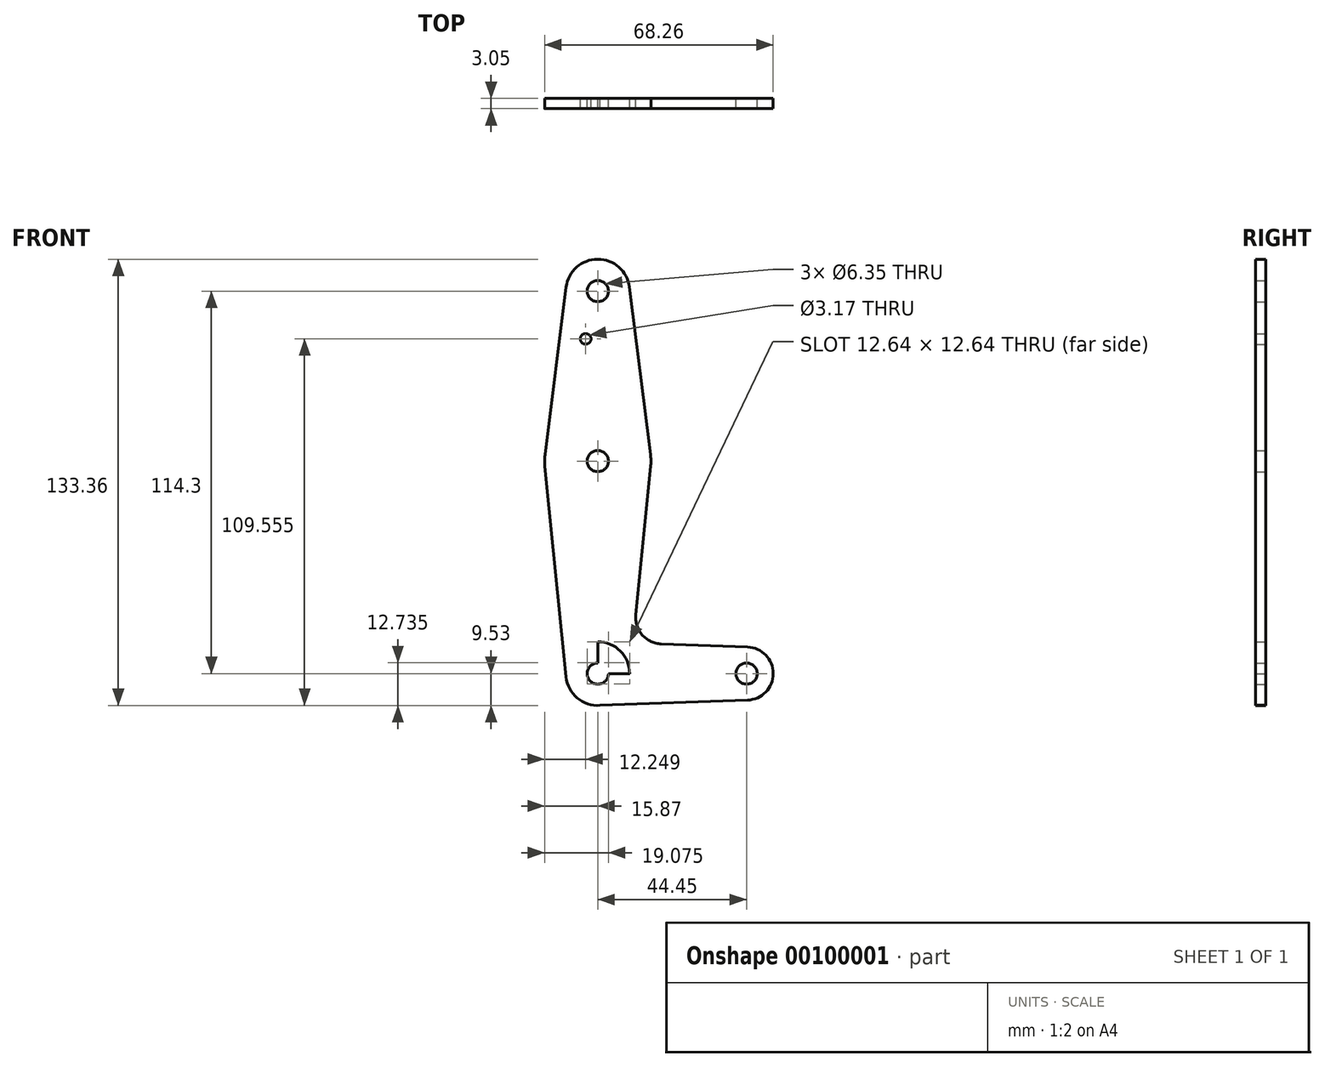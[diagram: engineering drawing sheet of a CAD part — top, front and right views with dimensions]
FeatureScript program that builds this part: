
annotation { "Feature Type Name" : "Feature", "Feature Type Description" : "" }
export const myFeature = defineFeature(function(context is Context, id is Id, definition is map)
    precondition{}
    {
        {
            var Q0;
            Q0=qCreatedBy(makeId("Front.planeOp"),FACE);
            var sketch = newSketch(context, id + "F0", { "sketchPlane" : qUnion([Q0])});
            skCircle(sketch, "E0", {"center": v(0, 114.3) * mm, "radius": 9.53 * mm});
            skCircle(sketch, "E1", {"center": v(0, 63.5) * mm, "radius": 15.88 * mm});
            skCircle(sketch, "E2", {"center": v(0, 0) * mm, "radius": 9.53 * mm});
            skCircle(sketch, "E3", {"center": v(44.45, 0) * mm, "radius": 7.94 * mm});
            skLineSegment(sketch, "E4", {"start": v(0, 114.3) * mm, "end": v(0, 63.5) * mm});
            skLineSegment(sketch, "E5", {"start": v(0, 63.5) * mm, "end": v(0, 0) * mm});
            skLineSegment(sketch, "E6", {"start": v(0, 0) * mm, "end": v(44.45, 0) * mm});
            skLineSegment(sketch, "E7", {"start": v(7.52, 77.48) * mm, "end": v(7.04, 75.9) * mm});
            skLineSegment(sketch, "E8", {"start": v(7.04, 75.9) * mm, "end": v(7.52, 77.48) * mm});
            skLineSegment(sketch, "E9", {"start": v(0, -9.53) * mm, "end": v(44.73, -7.93) * mm});
            skLineSegment(sketch, "E10", {"start": v(18.97, 8.85) * mm, "end": v(44.73, 7.93) * mm});
            skLineSegment(sketch, "E11", {"start": v(15.8, 61.91) * mm, "end": v(11.34, 17.6) * mm});
            skLineSegment(sketch, "E12", {"start": v(-15.8, 61.91) * mm, "end": v(-9.48, -0.95) * mm});
            skLineSegment(sketch, "E13", {"start": v(9.45, 115.5) * mm, "end": v(15.75, 65.48) * mm});
            skLineSegment(sketch, "E14", {"start": v(-9.45, 115.5) * mm, "end": v(-15.75, 65.48) * mm});
            skCircle(sketch, "E15", {"center": v(0, 114.3) * mm, "radius": 3.18 * mm});
            skCircle(sketch, "E16", {"center": v(0, 63.5) * mm, "radius": 3.18 * mm});
            skCircle(sketch, "E17", {"center": v(0, 0) * mm, "radius": 3.18 * mm});
            skCircle(sketch, "E18", {"center": v(44.45, 0) * mm, "radius": 3.18 * mm});
            skCircle(sketch, "E19", {"center": v(-3.62, 100.03) * mm, "radius": 1.59 * mm});
            skArc(sketch, "E20.filletArc", {"start": v(11.34, 17.6) * mm, "mid": v(13.26, 11.57) * mm, "end": v(18.97, 8.85) * mm});
            skSolve(sketch);
        }
        {
            var Q0;
            Q0 = qSketchRegion(id + "F0", true);
            extrude(context, id + "F1", {"entities" : qUnion([Q0]), "depth" : 3.05 * mm});
        }
        {
            var Q0;
            Q0 = qSketchRegion(id + "F0", true);
            extrude(context, id + "F2", {"entities" : qUnion([Q0]), "operationType" : NewBodyOperationType.ADD, "depth" : 3.05 * mm});
        }
    });
